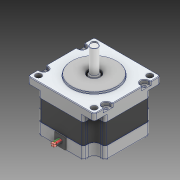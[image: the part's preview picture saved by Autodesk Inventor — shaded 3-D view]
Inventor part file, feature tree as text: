
AUTODESK INVENTOR PART (.ipt)
format: ipt  version: 2020 (Build 240168000, 168)  size: 450,048 bytes
history: native  units: in
note: dims shown in document units (in); Inventor stores cm internally (conversion verified against a paired STEP export)
features: other x10, extrude x1, sketch x1
ambient origin geometry x8: Origin, YZ Plane, XZ Plane, XY Plane, X Axis, Y Axis, Z Axis, Center Point
bodies: Solid1 (feature_tree), Solid2 (feature_tree), Solid3 (feature_tree), Solid4 (feature_tree), Solid5 (feature_tree), Solid6 (feature_tree), Solid7 (feature_tree), Solid8 (feature_tree), Solid9 (feature_tree), Solid10 (feature_tree)
feature tree (12):
  extrude  "Extrusion1"  Depth=0.0787in TaperAngle=0.0deg
  sketch  "Sketch1"  dims[d0=0.6693in d1=0.0in d2=0.0787in d3=0.0in]
  other  "Boss-Extrude7"
  other  "Boss-Extrude8[1]"
  other  "Boss-Extrude8[2]"
  other  "Boss-Extrude8[3]"
  other  "Boss-Extrude8[4]"
  other  "Boss-Extrude9[1]"
  other  "Boss-Extrude9[2]"
  other  "Boss-Extrude9[3]"
  other  "Boss-Extrude9[4]"
  other  "M3 Tapped Hole2"
